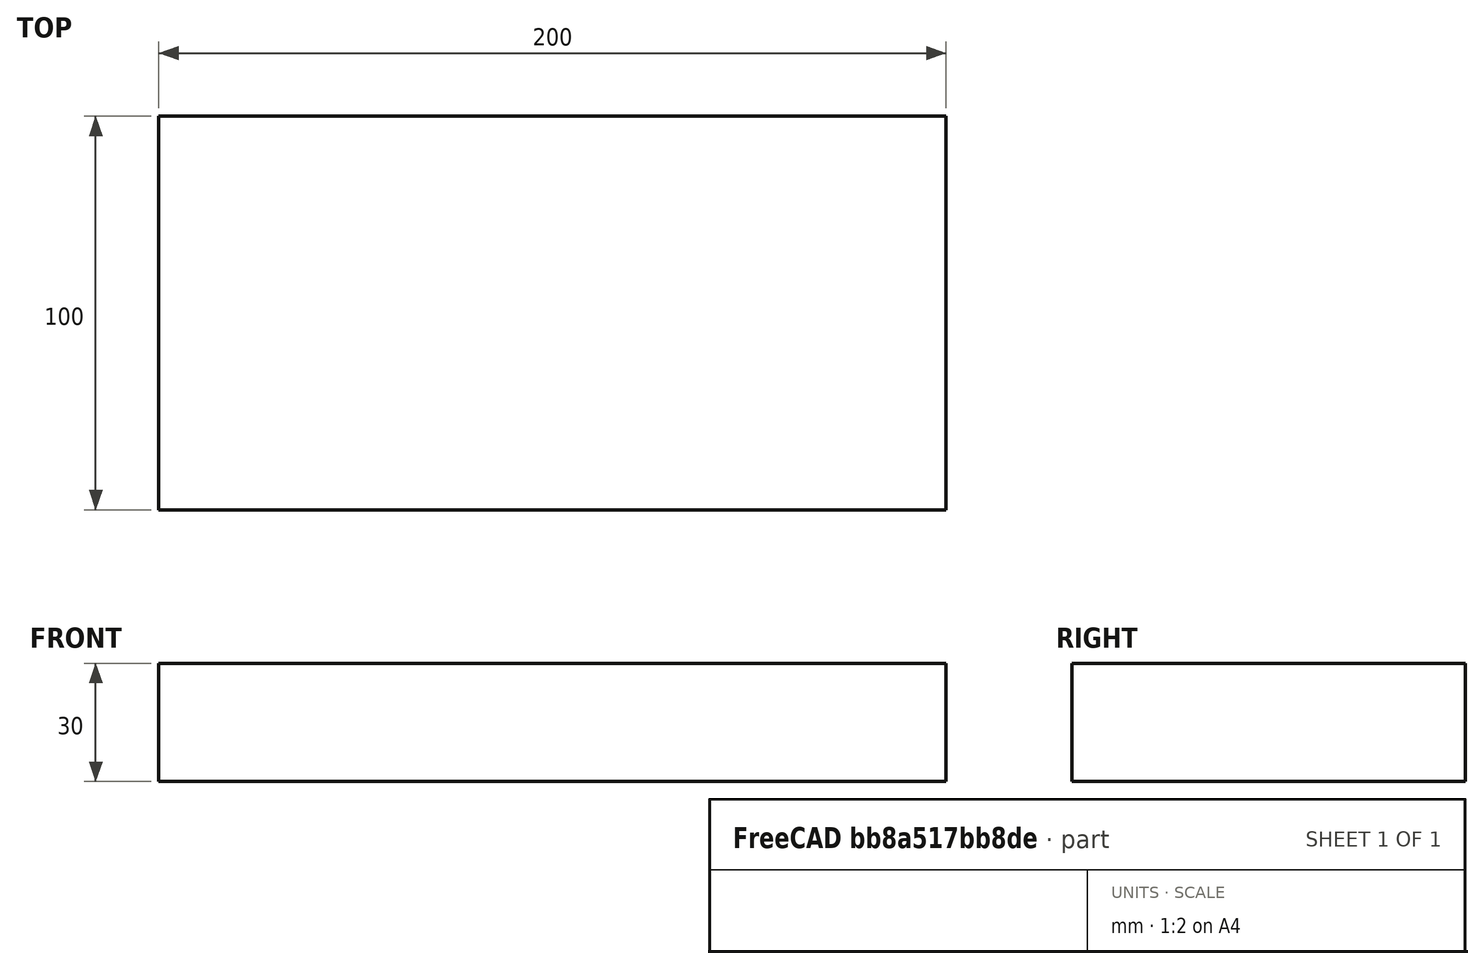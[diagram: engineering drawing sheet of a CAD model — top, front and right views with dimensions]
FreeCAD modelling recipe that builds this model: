
FCSTD DOCUMENT  (FreeCAD 0.19R24276 (Git))
Label: bldc_holder_p1_200x100x30
License: All rights reserved
LicenseURL: http://en.wikipedia.org/wiki/All_rights_reserved
objects: Sketcher::SketchObject×1, PartDesign::Pad×1, PartDesign::Body×1
note: 4 computed .brp shape members not serialized (recipe doc carries the construction recipe); baked Part::Feature solids carry a one-line shape summary decoded from their .brp

FEATURE [Sketcher::SketchObject] Sketch
  FullyConstrained = true
  MapMode = 5
  Support = -> [XY_Plane]
  sketch-geometry (4):
    g0: LineSegment StartX=0 StartY=0 StartZ=0 EndX=200 EndY=0 EndZ=0
    g1: LineSegment StartX=200 StartY=0 StartZ=0 EndX=200 EndY=100 EndZ=0
    g2: LineSegment StartX=200 StartY=100 StartZ=0 EndX=0 EndY=100 EndZ=0
    g3: LineSegment StartX=0 StartY=100 StartZ=0 EndX=0 EndY=0 EndZ=0
  constraints (11):
    c: Coincident(g0,g1)
    c: Coincident(g1,g2)
    c: Coincident(g2,g3)
    c: Coincident(g3,g0)
    c: Horizontal(g0)
    c: Horizontal(g2)
    c: Vertical(g1)
    c: Vertical(g3)
    c: Coincident(g0,g-1)
    c: DistanceX(g0,g0) = 200
    c: DistanceY(g1,g1) = 100
FEATURE [PartDesign::Pad] Pad
  Direction = (1,1,1)
  Length = 30
  Length2 = 100
  Profile = -> Sketch
  Type = 0
FEATURE [PartDesign::Body] Body
  Group = -> [Sketch,Pad]
  Origin = -> Origin
  Tip = -> Pad
